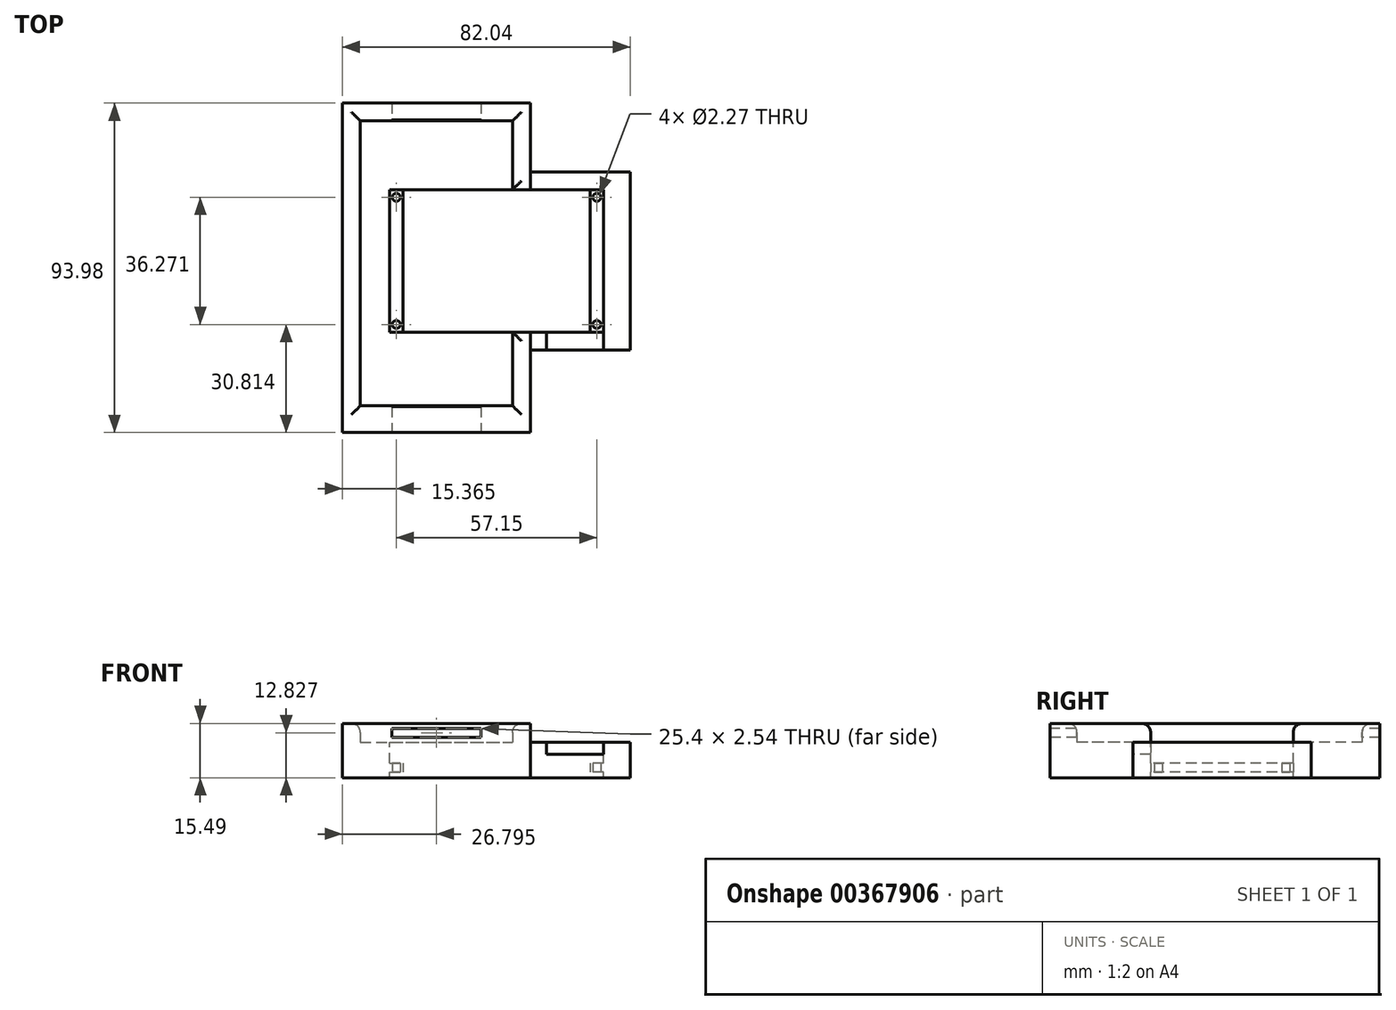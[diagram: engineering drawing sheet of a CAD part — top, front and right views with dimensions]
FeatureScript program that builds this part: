
annotation { "Feature Type Name" : "Feature", "Feature Type Description" : "" }
export const myFeature = defineFeature(function(context is Context, id is Id, definition is map)
    precondition{}
    {
        {
            var Q0;
            Q0=qCreatedBy(makeId("Top.planeOp"),FACE);
            var sketch = newSketch(context, id + "F0", { "sketchPlane" : qUnion([Q0])});
            skLineSegment(sketch, "E0.bottom", {"start": v(-38.1, 25.4) * mm, "end": v(38.1, 25.4) * mm});
            skLineSegment(sketch, "E0.top", {"start": v(-38.1, -25.4) * mm, "end": v(38.1, -25.4) * mm});
            skLineSegment(sketch, "E0.left", {"start": v(-38.1, 25.4) * mm, "end": v(-38.1, -25.4) * mm});
            skLineSegment(sketch, "E0.right", {"start": v(38.1, 25.4) * mm, "end": v(38.1, -25.4) * mm});
            skSolve(sketch);
        }
        {
            var Q0;
            Q0=makeQuery(id+"F0.imprint","IMPRINT",FACE,{"disambiguationData":[TD([[makeQuery(id+"F0.imprint","IMPRINT",EDGE,{"derivedFrom":sQuery(id+"F0.wireOp",EDGE,"E0.bottom")}),-1.0]])]});
            extrude(context, id + "F1", {"entities" : qUnion([Q0]), "depth" : 20.32 * mm});
        }
        {
            var Q0;
            Q0=makeQuery(id+"F1.opExtrude","CAP_FACE",FACE,{"disambiguationData":[OSD([sQuery(id+"F0.wireOp",EDGE,"E0.bottom"),sQuery(id+"F0.wireOp",EDGE,"E0.top"),sQuery(id+"F0.wireOp",EDGE,"E0.left"),sQuery(id+"F0.wireOp",EDGE,"E0.right")])],"isStart":false});
            var sketch = newSketch(context, id + "F2", { "sketchPlane" : qUnion([Q0])});
            skLineSegment(sketch, "E1.bottom", {"start": v(-30.48, 20.32) * mm, "end": v(30.48, 20.32) * mm});
            skLineSegment(sketch, "E1.top", {"start": v(-30.48, -20.32) * mm, "end": v(30.48, -20.32) * mm});
            skLineSegment(sketch, "E1.left", {"start": v(-30.48, 20.32) * mm, "end": v(-30.48, -20.32) * mm});
            skLineSegment(sketch, "E1.right", {"start": v(30.48, 20.32) * mm, "end": v(30.48, -20.32) * mm});
            skSolve(sketch);
        }
        {
            var Q0;
            Q0 = qSketchRegion(id + "F2", true);
            extrude(context, id + "F3", {"entities" : qUnion([Q0]), "operationType" : NewBodyOperationType.REMOVE, "oppositeDirection" : true, "depth" : 17.27 * mm});
        }
        {
            var Q0;
            Q0=makeQuery(id+"F3.boolean.opBoolean","COPY",FACE,{"derivedFrom":makeQuery(id+"F3.opExtrude","CAP_FACE",FACE,{"disambiguationData":[OSD([sQuery(id+"F2.wireOp",EDGE,"E1.bottom"),sQuery(id+"F2.wireOp",EDGE,"E1.top"),sQuery(id+"F2.wireOp",EDGE,"E1.left"),sQuery(id+"F2.wireOp",EDGE,"E1.right"),sQuery(id+"F2.wireOp",EDGE,"rvkAKrci-OVvJ-b99a-57h3-4Hy4aDSIWGUz.top"),sQuery(id+"F2.wireOp",EDGE,"rvkAKrci-OVvJ-b99a-57h3-4Hy4aDSIWGUz.left"),sQuery(id+"F2.wireOp",EDGE,"rvkAKrci-OVvJ-b99a-57h3-4Hy4aDSIWGUz.right")])],"isStart":false})});
            cPlane(context, id + "F4", {"entities" : qUnion([Q0]), "cplaneType" : CPlaneType.OFFSET, "offset" : 8.7 * mm, "width" : 152.4 * mm, "height" : 152.4 * mm});
        }
        {
            var Q0;
            Q0=qCreatedBy(id+"F4.planeOp",FACE);
            var sketch = newSketch(context, id + "F5", { "sketchPlane" : qUnion([Q0])});
            skLineSegment(sketch, "E2.0", {"start": v(-30.48, 20.32) * mm, "end": v(-30.48, -20.32) * mm});
            skLineSegment(sketch, "E3", {"start": v(-30.48, 20.32) * mm, "end": v(-26.67, 20.32) * mm});
            skLineSegment(sketch, "E4", {"start": v(-30.48, -20.32) * mm, "end": v(-26.67, -20.32) * mm});
            skLineSegment(sketch, "E5", {"start": v(-26.67, -20.32) * mm, "end": v(-26.67, 20.32) * mm});
            skCircle(sketch, "E6", {"center": v(-28.57, 18.14) * mm, "radius": 1.14 * mm});
            skPoint(sketch, "E6.centerSnap0", {"position": v(-28.57, 20.32) * mm});
            skCircle(sketch, "E7.MirrorC", {"center": v(-28.57, -18.14) * mm, "radius": 1.14 * mm});
            skLineSegment(sketch, "E8.MirrorCS", {"start": v(30.48, 20.32) * mm, "end": v(26.67, 20.32) * mm});
            skCircle(sketch, "E9.MirrorC", {"center": v(28.57, 18.14) * mm, "radius": 1.14 * mm});
            skLineSegment(sketch, "E10.MirrorCS", {"start": v(26.67, -20.32) * mm, "end": v(26.67, 20.32) * mm});
            skCircle(sketch, "E11.MirrorC", {"center": v(28.57, -18.14) * mm, "radius": 1.14 * mm});
            skLineSegment(sketch, "E12.MirrorCS", {"start": v(30.48, 20.32) * mm, "end": v(30.48, -20.32) * mm});
            skLineSegment(sketch, "E13.MirrorCS", {"start": v(30.48, -20.32) * mm, "end": v(26.67, -20.32) * mm});
            skPoint(sketch, "E14.MirrorP", {"position": v(28.57, 20.32) * mm});
            skSolve(sketch);
        }
        {
            var Q0;
            Q0 = qSketchRegion(id + "F5", true);
            extrude(context, id + "F6", {"entities" : qUnion([Q0]), "operationType" : NewBodyOperationType.ADD, "depth" : 2.54 * mm});
        }
        {
            var Q0;
            Q0=makeQuery(id+"F6.opExtrude","CAP_FACE",FACE,{"disambiguationData":[OSD([sQuery(id+"F5.wireOp",EDGE,"E8.MirrorCS"),sQuery(id+"F5.wireOp",EDGE,"E9.MirrorC"),sQuery(id+"F5.wireOp",EDGE,"E10.MirrorCS"),sQuery(id+"F5.wireOp",EDGE,"E11.MirrorC"),sQuery(id+"F5.wireOp",EDGE,"E12.MirrorCS"),sQuery(id+"F5.wireOp",EDGE,"E13.MirrorCS")])],"isStart":false});
            cPlane(context, id + "F7", {"entities" : qUnion([Q0]), "cplaneType" : CPlaneType.OFFSET, "offset" : 2.54 * mm, "width" : 152.4 * mm, "height" : 152.4 * mm});
        }
        {
            var Q0;
            Q0=qCreatedBy(id+"F7.planeOp",FACE);
            var sketch = newSketch(context, id + "F8", { "sketchPlane" : qUnion([Q0])});
            skLineSegment(sketch, "E15.bottom", {"start": v(30.48, -20.32) * mm, "end": v(14.22, -20.32) * mm});
            skLineSegment(sketch, "E15.top", {"start": v(30.48, -25.4) * mm, "end": v(14.22, -25.4) * mm});
            skLineSegment(sketch, "E15.left", {"start": v(30.48, -20.32) * mm, "end": v(30.48, -25.4) * mm});
            skLineSegment(sketch, "E15.right", {"start": v(14.22, -20.32) * mm, "end": v(14.22, -25.4) * mm});
            skSolve(sketch);
        }
        {
            var Q0;
            Q0 = qSketchRegion(id + "F8", true);
            var Q1;
            Q1=makeQuery(id+"F1.opExtrude","CAP_FACE",FACE,{"disambiguationData":[OSD([sQuery(id+"F0.wireOp",EDGE,"E0.bottom"),sQuery(id+"F0.wireOp",EDGE,"E0.top"),sQuery(id+"F0.wireOp",EDGE,"E0.left"),sQuery(id+"F0.wireOp",EDGE,"E0.right")])],"isStart":false});
            extrude(context, id + "F9", {"entities" : qUnion([Q0]), "operationType" : NewBodyOperationType.REMOVE, "endBound" : BoundingType.UP_TO_SURFACE, "endBoundEntityFace" : qUnion([Q1]), "depth" : 25.4 * mm});
        }
        {
            var Q0;
            Q0=makeQuery(id+"F1.opExtrude","CAP_FACE",FACE,{"disambiguationData":[OSD([sQuery(id+"F0.wireOp",EDGE,"E0.bottom"),sQuery(id+"F0.wireOp",EDGE,"E0.top"),sQuery(id+"F0.wireOp",EDGE,"E0.left"),sQuery(id+"F0.wireOp",EDGE,"E0.right")])],"isStart":false});
            var sketch = newSketch(context, id + "F10", { "sketchPlane" : qUnion([Q0])});
            skLineSegment(sketch, "E16.bottom", {"start": v(-38.86, 39.95) * mm, "end": v(4.57, 39.95) * mm});
            skLineSegment(sketch, "E16.top", {"start": v(-38.86, -41.33) * mm, "end": v(4.57, -41.33) * mm});
            skLineSegment(sketch, "E16.left", {"start": v(-38.86, 39.95) * mm, "end": v(-38.86, -41.33) * mm});
            skLineSegment(sketch, "E16.right", {"start": v(4.57, 39.95) * mm, "end": v(4.57, 20.15) * mm});
            skLineSegment(sketch, "E17.bottom", {"start": v(-43.94, 45.03) * mm, "end": v(9.65, 45.03) * mm});
            skLineSegment(sketch, "E17.top", {"start": v(-43.94, -48.95) * mm, "end": v(9.65, -48.95) * mm});
            skLineSegment(sketch, "E17.left", {"start": v(-43.94, 45.03) * mm, "end": v(-43.94, -48.95) * mm});
            skLineSegment(sketch, "E17.right", {"start": v(9.65, 45.03) * mm, "end": v(9.65, 20.32) * mm});
            skLineSegment(sketch, "E18.0", {"start": v(4.57, 20.32) * mm, "end": v(9.65, 20.32) * mm});
            skLineSegment(sketch, "E19.0", {"start": v(4.57, -20.32) * mm, "end": v(9.65, -20.32) * mm});
            skLineSegment(sketch, "E20", {"start": v(4.57, -20.32) * mm, "end": v(4.57, -41.33) * mm});
            skPoint(sketch, "E21.orphan", {"position": v(-30.48, -20.32) * mm});
            skPoint(sketch, "E22.end.orphan", {"position": v(14.22, -20.32) * mm});
            skPoint(sketch, "E23.orphan", {"position": v(-30.48, 20.32) * mm});
            skPoint(sketch, "E24.end.orphan", {"position": v(30.48, 20.32) * mm});
            skLineSegment(sketch, "E25.trimOffspring", {"start": v(9.65, -20.32) * mm, "end": v(9.65, -48.95) * mm});
            skSolve(sketch);
        }
        {
            var Q0;
            Q0 = qSketchRegion(id + "F10", true);
            extrude(context, id + "F11", {"entities" : qUnion([Q0]), "operationType" : NewBodyOperationType.ADD, "depth" : 5.33 * mm});
        }
        {
            var Q0;
            Q0=makeQuery(id+"F1.opExtrude","CAP_FACE",FACE,{"disambiguationData":[OSD([sQuery(id+"F0.wireOp",EDGE,"E0.bottom"),sQuery(id+"F0.wireOp",EDGE,"E0.top"),sQuery(id+"F0.wireOp",EDGE,"E0.left"),sQuery(id+"F0.wireOp",EDGE,"E0.right")])],"isStart":true});
            var sketch = newSketch(context, id + "F12", { "sketchPlane" : qUnion([Q0])});
            skLineSegment(sketch, "E26.0", {"start": v(-43.94, -45.03) * mm, "end": v(-43.94, 48.95) * mm});
            skLineSegment(sketch, "E27.0", {"start": v(-43.94, 48.95) * mm, "end": v(9.65, 48.95) * mm});
            skLineSegment(sketch, "E28.0", {"start": v(9.65, 25.4) * mm, "end": v(9.65, 48.95) * mm});
            skLineSegment(sketch, "E29.0", {"start": v(-38.1, 25.4) * mm, "end": v(9.65, 25.4) * mm});
            skLineSegment(sketch, "E30.0", {"start": v(-38.1, -25.4) * mm, "end": v(9.65, -25.4) * mm});
            skLineSegment(sketch, "E31.0", {"start": v(9.65, -45.03) * mm, "end": v(9.65, -25.4) * mm});
            skLineSegment(sketch, "E32.0", {"start": v(-43.94, -45.03) * mm, "end": v(9.65, -45.03) * mm});
            skLineSegment(sketch, "E33.0", {"start": v(-38.1, -25.4) * mm, "end": v(-38.1, 25.4) * mm});
            skPoint(sketch, "E34.orphan", {"position": v(38.1, 25.4) * mm});
            skPoint(sketch, "E35.orphan", {"position": v(38.1, -25.4) * mm});
            skSolve(sketch);
        }
        {
            var Q0;
            Q0 = qSketchRegion(id + "F12", true);
            var Q1;
            Q1=makeQuery(id+"F11.opExtrude","CAP_FACE",FACE,{"disambiguationData":[OSD([sQuery(id+"F10.wireOp",EDGE,"E16.bottom"),sQuery(id+"F10.wireOp",EDGE,"E16.top"),sQuery(id+"F10.wireOp",EDGE,"E16.left"),sQuery(id+"F10.wireOp",EDGE,"E16.right"),sQuery(id+"F10.wireOp",EDGE,"E17.bottom"),sQuery(id+"F10.wireOp",EDGE,"E17.top"),sQuery(id+"F10.wireOp",EDGE,"E17.left"),sQuery(id+"F10.wireOp",EDGE,"E17.right"),sQuery(id+"F10.wireOp",EDGE,"E18.0"),sQuery(id+"F10.wireOp",EDGE,"E19.0"),sQuery(id+"F10.wireOp",EDGE,"E20"),sQuery(id+"F10.wireOp",EDGE,"E25.trimOffspring")])],"isStart":true});
            extrude(context, id + "F13", {"entities" : qUnion([Q0]), "operationType" : NewBodyOperationType.ADD, "endBound" : BoundingType.UP_TO_SURFACE, "oppositeDirection" : true, "endBoundEntityFace" : qUnion([Q1]), "depth" : 25.4 * mm});
        }
        {
            var Q0;
            {var subQ0=sQuery(id+"F2.wireOp",EDGE,"E1.bottom");Q0=makeQuery(id+"F11.boolean.opBoolean","SPLIT",EDGE,{"disambiguationData":[TD([makeQuery(id+"F3.boolean.opBoolean","COPY",FACE,{"derivedFrom":makeQuery(id+"F3.opExtrude","SWEPT_FACE",FACE,{"disambiguationData":[OSD([sQuery(id+"F2.wireOp",EDGE,"E1.left")])]})})])],"derivedFrom":makeQuery(id+"F3.boolean.opBoolean","COPY",EDGE,{"derivedFrom":makeQuery(id+"F3.opExtrude","CAP_EDGE",EDGE,{"disambiguationData":[OSD([subQ0])],"isStart":true})})});}
            var Q1;
            Q1=makeQuery(id+"F3.boolean.opBoolean","COPY",EDGE,{"derivedFrom":makeQuery(id+"F3.opExtrude","CAP_EDGE",EDGE,{"disambiguationData":[OSD([sQuery(id+"F2.wireOp",EDGE,"E1.left")])],"isStart":true})});
            var Q2;
            Q2=makeQuery(id+"F9.boolean.opBoolean","MERGE",EDGE,{"derivedFrom":[makeQuery(id+"F3.boolean.opBoolean","COPY",EDGE,{"derivedFrom":makeQuery(id+"F3.opExtrude","CAP_EDGE",EDGE,{"disambiguationData":[OSD([sQuery(id+"F2.wireOp",EDGE,"E1.right")])],"isStart":true})}),makeQuery(id+"F9.opExtrude","TWEAK_EDGE",EDGE,{"derivedFrom":[makeQuery(id+"F1.opExtrude","CAP_FACE",FACE,{"disambiguationData":[OSD([sQuery(id+"F0.wireOp",EDGE,"E0.bottom"),sQuery(id+"F0.wireOp",EDGE,"E0.top"),sQuery(id+"F0.wireOp",EDGE,"E0.left"),sQuery(id+"F0.wireOp",EDGE,"E0.right")])],"isStart":false}),makeQuery(id+"F8.imprint","IMPRINT",EDGE,{"derivedFrom":sQuery(id+"F8.wireOp",EDGE,"E15.left")})]})]});
            var Q3;
            Q3=makeQuery(id+"F11.opExtrude","CAP_EDGE",EDGE,{"disambiguationData":[OSD([sQuery(id+"F10.wireOp",EDGE,"E16.bottom")])],"isStart":false});
            var Q4;
            Q4=makeQuery(id+"F11.opExtrude","CAP_EDGE",EDGE,{"disambiguationData":[OSD([sQuery(id+"F10.wireOp",EDGE,"E16.left")])],"isStart":false});
            var Q5;
            Q5=makeQuery(id+"F11.opExtrude","CAP_EDGE",EDGE,{"disambiguationData":[OSD([sQuery(id+"F10.wireOp",EDGE,"E16.top")])],"isStart":false});
            var Q6;
            Q6=makeQuery(id+"F11.opExtrude","CAP_EDGE",EDGE,{"disambiguationData":[OSD([sQuery(id+"F10.wireOp",EDGE,"E20")])],"isStart":false});
            var Q7;
            Q7=makeQuery(id+"F11.opExtrude","CAP_EDGE",EDGE,{"disambiguationData":[OSD([sQuery(id+"F10.wireOp",EDGE,"E16.right")])],"isStart":false});
            var Q8;
            Q8=makeQuery(id+"F9.boolean.opBoolean","COPY",EDGE,{"derivedFrom":makeQuery(id+"F9.opExtrude","CAP_EDGE",EDGE,{"disambiguationData":[OSD([sQuery(id+"F8.wireOp",EDGE,"E15.bottom")])],"isStart":true})});
            var Q9;
            {var subQ0=sQuery(id+"F2.wireOp",EDGE,"E1.top");Q9=makeQuery(id+"F11.boolean.opBoolean","SPLIT",EDGE,{"disambiguationData":[TD([makeQuery(id+"F9.boolean.opBoolean","COPY",FACE,{"derivedFrom":makeQuery(id+"F9.opExtrude","SWEPT_FACE",FACE,{"disambiguationData":[OSD([sQuery(id+"F8.wireOp",EDGE,"E15.right")])]})})])],"derivedFrom":makeQuery(id+"F3.boolean.opBoolean","COPY",EDGE,{"derivedFrom":makeQuery(id+"F3.opExtrude","CAP_EDGE",EDGE,{"disambiguationData":[OSD([subQ0])],"isStart":true})})});}
            var Q10;
            {var subQ0=sQuery(id+"F2.wireOp",EDGE,"E1.top");Q10=makeQuery(id+"F11.boolean.opBoolean","SPLIT",EDGE,{"disambiguationData":[TD([makeQuery(id+"F3.boolean.opBoolean","COPY",FACE,{"derivedFrom":makeQuery(id+"F3.opExtrude","SWEPT_FACE",FACE,{"disambiguationData":[OSD([sQuery(id+"F2.wireOp",EDGE,"E1.left")])]})})])],"derivedFrom":makeQuery(id+"F3.boolean.opBoolean","COPY",EDGE,{"derivedFrom":makeQuery(id+"F3.opExtrude","CAP_EDGE",EDGE,{"disambiguationData":[OSD([subQ0])],"isStart":true})})});}
            var Q11;
            {var subQ0=sQuery(id+"F2.wireOp",EDGE,"E1.bottom");Q11=makeQuery(id+"F11.boolean.opBoolean","SPLIT",EDGE,{"disambiguationData":[TD([makeQuery(id+"F3.boolean.opBoolean","COPY",FACE,{"derivedFrom":makeQuery(id+"F3.opExtrude","SWEPT_FACE",FACE,{"disambiguationData":[OSD([sQuery(id+"F2.wireOp",EDGE,"E1.right")])]})})])],"derivedFrom":makeQuery(id+"F3.boolean.opBoolean","COPY",EDGE,{"derivedFrom":makeQuery(id+"F3.opExtrude","CAP_EDGE",EDGE,{"disambiguationData":[OSD([subQ0])],"isStart":true})})});}
            var Q12;
            Q12=makeQuery(id+"F11.opExtrude","CAP_EDGE",EDGE,{"disambiguationData":[OSD([sQuery(id+"F10.wireOp",EDGE,"E18.0")])],"isStart":false});
            var Q13;
            Q13=makeQuery(id+"F11.opExtrude","CAP_EDGE",EDGE,{"disambiguationData":[OSD([sQuery(id+"F10.wireOp",EDGE,"E19.0")])],"isStart":false});
            fillet(context, id + "F14", {"entities" : qUnion([Q0, Q1, Q2, Q3, Q4, Q5, Q6, Q7, Q8, Q9, Q10, Q11, Q12, Q13]), "radius" : 2.54 * mm, "tangentPropagation" : true, "allowEdgeOverflow" : false});
        }
        {
            var Q0;
            Q0=makeQuery(id+"F1.opExtrude","SWEPT_FACE",FACE,{"disambiguationData":[OSD([sQuery(id+"F0.wireOp",EDGE,"E0.right")])]});
            var sketch = newSketch(context, id + "F15", { "sketchPlane" : qUnion([Q0])});
            skPoint(sketch, "E36.0", {"position": v(-48.95, 0) * mm});
            skLineSegment(sketch, "E37.0", {"start": v(45.03, 25.65) * mm, "end": v(45.03, 0) * mm, "construction": true});
            skLineSegment(sketch, "E38.bottom", {"start": v(-48.95, 0) * mm, "end": v(45.03, 0) * mm});
            skLineSegment(sketch, "E38.top", {"start": v(-48.95, 10.16) * mm, "end": v(45.03, 10.16) * mm});
            skLineSegment(sketch, "E38.left", {"start": v(-48.95, 0) * mm, "end": v(-48.95, 10.16) * mm});
            skLineSegment(sketch, "E38.right", {"start": v(45.03, 0) * mm, "end": v(45.03, 10.16) * mm});
            skSolve(sketch);
        }
        {
            var Q0;
            Q0 = qSketchRegion(id + "F15", true);
            var Q1;
            Q1=makeQuery(id+"F13.boolean.opBoolean","MERGE",FACE,{"derivedFrom":[makeQuery(id+"F11.opExtrude","SWEPT_FACE",FACE,{"disambiguationData":[OSD([sQuery(id+"F10.wireOp",EDGE,"E17.left")])]}),makeQuery(id+"F13.opExtrude","SWEPT_FACE",FACE,{"disambiguationData":[OSD([sQuery(id+"F12.wireOp",EDGE,"E26.0")])]})]});
            extrude(context, id + "F16", {"entities" : qUnion([Q0]), "operationType" : NewBodyOperationType.REMOVE, "endBound" : BoundingType.UP_TO_SURFACE, "oppositeDirection" : true, "endBoundEntityFace" : qUnion([Q1]), "depth" : 25.4 * mm});
        }
        {
            var Q0;
            Q0=makeQuery(id+"F13.boolean.opBoolean","MERGE",FACE,{"derivedFrom":[makeQuery(id+"F11.opExtrude","SWEPT_FACE",FACE,{"disambiguationData":[OSD([sQuery(id+"F10.wireOp",EDGE,"E17.top")])]}),makeQuery(id+"F13.opExtrude","SWEPT_FACE",FACE,{"disambiguationData":[OSD([sQuery(id+"F12.wireOp",EDGE,"E27.0")])]})]});
            var sketch = newSketch(context, id + "F17", { "sketchPlane" : qUnion([Q0])});
            skLineSegment(sketch, "E39.bottom", {"start": v(-29.85, 24.26) * mm, "end": v(-4.45, 24.26) * mm});
            skLineSegment(sketch, "E39.top", {"start": v(-29.85, 21.72) * mm, "end": v(-4.45, 21.72) * mm});
            skLineSegment(sketch, "E39.left", {"start": v(-29.85, 24.26) * mm, "end": v(-29.85, 21.72) * mm});
            skLineSegment(sketch, "E39.right", {"start": v(-4.45, 24.26) * mm, "end": v(-4.45, 21.72) * mm});
            skLineSegment(sketch, "E40", {"start": v(-17.14, 25.65) * mm, "end": v(-17.14, 10.16) * mm, "construction": true});
            skSolve(sketch);
        }
        {
            var Q0;
            Q0 = qSketchRegion(id + "F17", true);
            var Q1;
            Q1=makeQuery(id+"F13.boolean.opBoolean","MERGE",FACE,{"derivedFrom":[makeQuery(id+"F11.opExtrude","SWEPT_FACE",FACE,{"disambiguationData":[OSD([sQuery(id+"F10.wireOp",EDGE,"E17.bottom")])]}),makeQuery(id+"F13.opExtrude","SWEPT_FACE",FACE,{"disambiguationData":[OSD([sQuery(id+"F12.wireOp",EDGE,"E32.0")])]})]});
            extrude(context, id + "F18", {"entities" : qUnion([Q0]), "operationType" : NewBodyOperationType.REMOVE, "endBound" : BoundingType.UP_TO_SURFACE, "oppositeDirection" : true, "endBoundEntityFace" : qUnion([Q1]), "depth" : 25.4 * mm});
        }
    });
